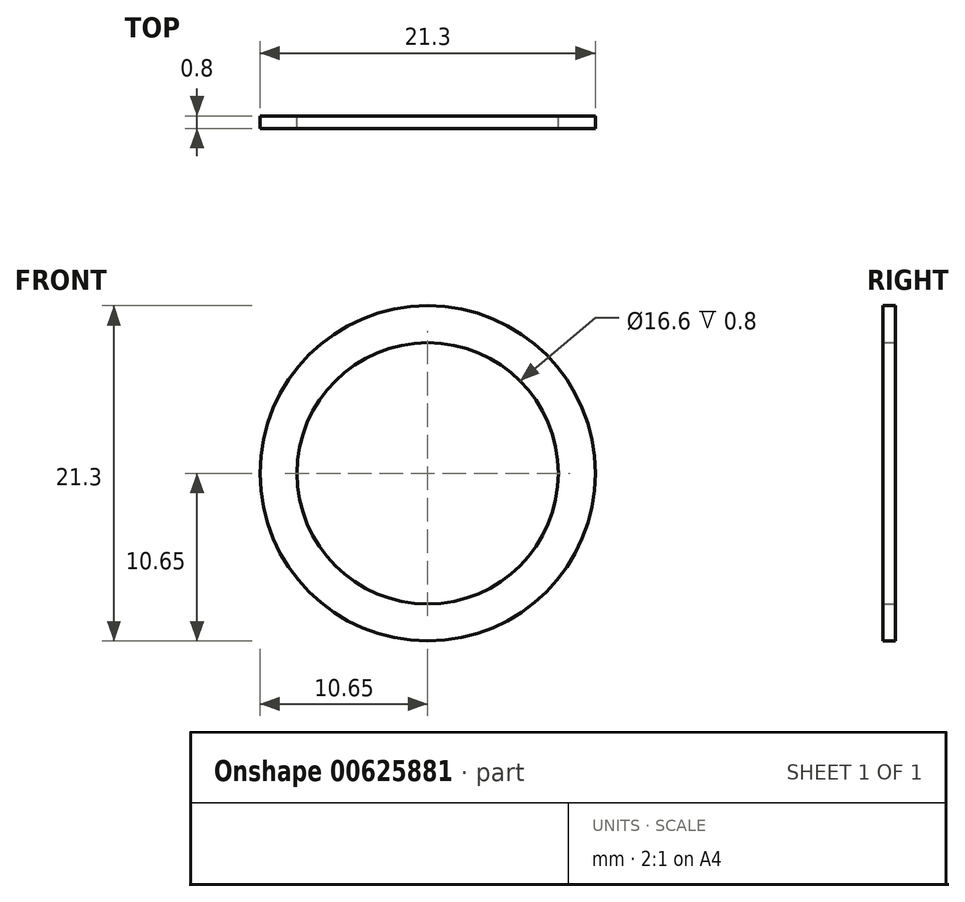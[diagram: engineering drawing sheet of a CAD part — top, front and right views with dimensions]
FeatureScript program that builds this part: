
annotation { "Feature Type Name" : "Feature", "Feature Type Description" : "" }
export const myFeature = defineFeature(function(context is Context, id is Id, definition is map)
    precondition{}
    {
        {
            var Q0;
            Q0=qCreatedBy(makeId("Front.planeOp"),FACE);
            var sketch = newSketch(context, id + "F0", { "sketchPlane" : qUnion([Q0])});
            skCircle(sketch, "E0", {"center": v(0, 0) * mm, "radius": 10.65 * mm});
            skSolve(sketch);
        }
        {
            var Q0;
            Q0=makeQuery(id+"F0.imprint","IMPRINT",FACE,{"disambiguationData":[TD([[makeQuery(id+"F0.imprint","IMPRINT",EDGE,{"derivedFrom":sQuery(id+"F0.wireOp",EDGE,"E0")}),1.0]])]});
            var sketch = newSketch(context, id + "F1", { "sketchPlane" : qUnion([Q0])});
            skCircle(sketch, "E1", {"center": v(0, 0) * mm, "radius": 8.3 * mm});
            skSolve(sketch);
        }
        {
            var Q0;
            Q0=makeQuery(id+"F1.imprint","IMPRINT",FACE,{"disambiguationData":[TD([[makeQuery(id+"F1.imprint","IMPRINT",EDGE,{"derivedFrom":sQuery(id+"F1.wireOp",EDGE,"E1")}),-1.0]])]});
            extrude(context, id + "F2", {"entities" : qUnion([Q0]), "depth" : 0.8 * mm, "offsetDistance" : 25 * mm});
        }
    });
